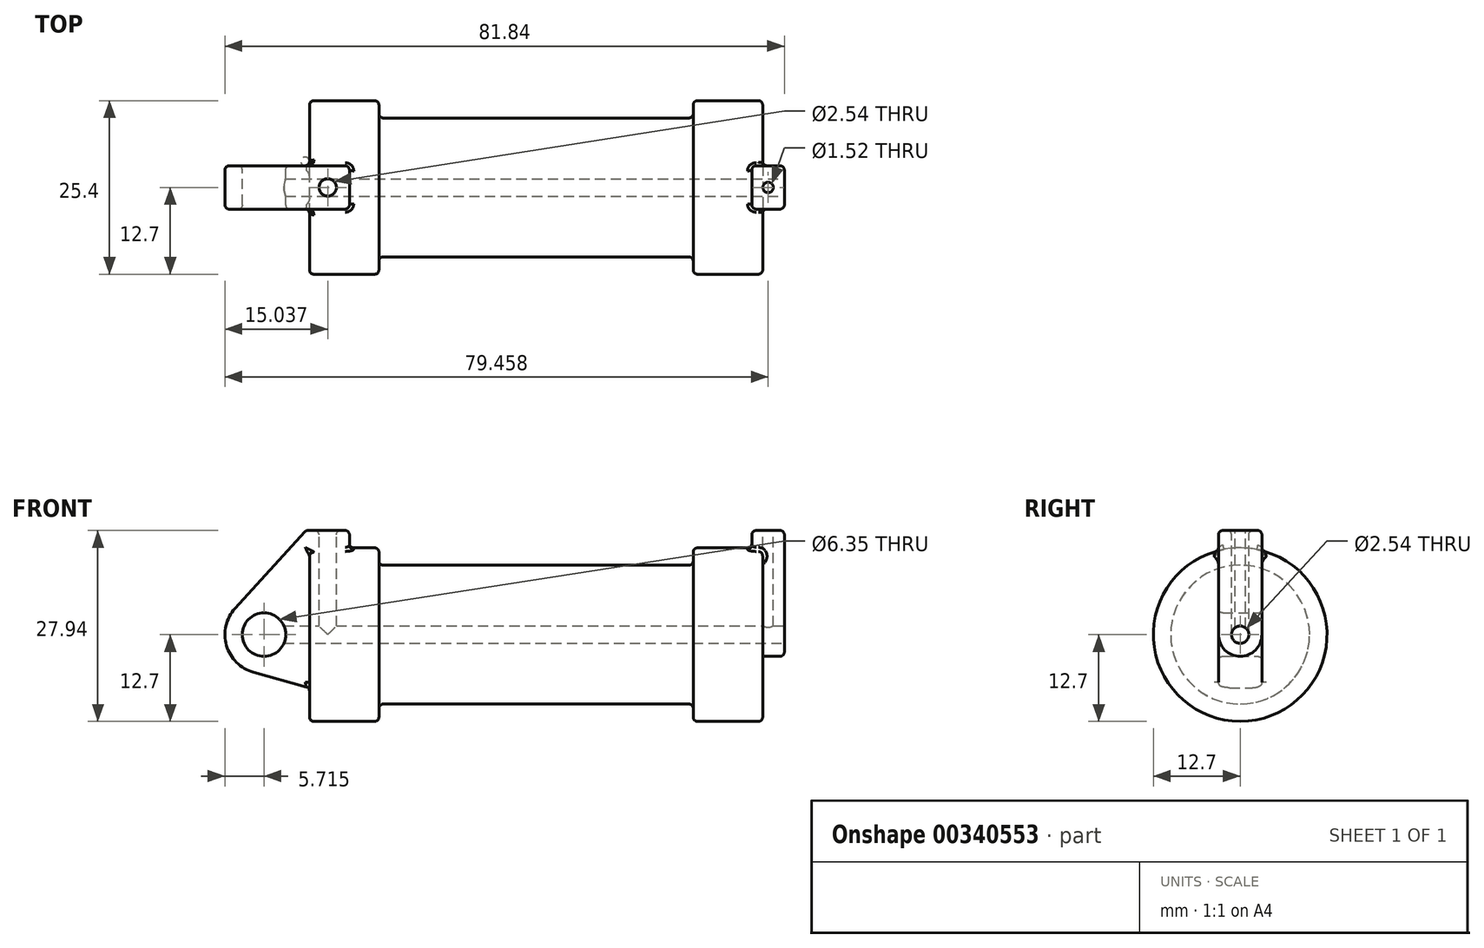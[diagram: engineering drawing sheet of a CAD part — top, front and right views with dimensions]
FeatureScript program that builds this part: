
annotation { "Feature Type Name" : "Feature", "Feature Type Description" : "" }
export const myFeature = defineFeature(function(context is Context, id is Id, definition is map)
    precondition{}
    {
        {
            var Q0;
            Q0=qCreatedBy(makeId("Front.planeOp"),FACE);
            var sketch = newSketch(context, id + "F0", { "sketchPlane" : qUnion([Q0])});
            skLineSegment(sketch, "E0", {"start": v(0, 0) * mm, "end": v(0, 12.7) * mm});
            skLineSegment(sketch, "E1", {"start": v(0, 12.7) * mm, "end": v(10.16, 12.7) * mm});
            skLineSegment(sketch, "E2", {"start": v(10.16, 12.7) * mm, "end": v(10.16, 10.16) * mm});
            skLineSegment(sketch, "E3", {"start": v(10.16, 10.16) * mm, "end": v(56.13, 10.16) * mm});
            skLineSegment(sketch, "E4", {"start": v(56.13, 10.16) * mm, "end": v(56.13, 12.7) * mm});
            skLineSegment(sketch, "E5", {"start": v(56.13, 12.7) * mm, "end": v(66.3, 12.7) * mm});
            skLineSegment(sketch, "E6", {"start": v(66.3, 12.7) * mm, "end": v(66.3, 0) * mm});
            skLineSegment(sketch, "E7", {"start": v(66.3, 0) * mm, "end": v(0, 0) * mm});
            skLineSegment(sketch, "E8", {"start": v(5.84, 15.24) * mm, "end": v(-0.5, 15.24) * mm});
            skLineSegment(sketch, "E9", {"start": v(-0.5, 15.24) * mm, "end": v(-10.88, 3.85) * mm});
            skLineSegment(sketch, "E10", {"start": v(0, 0) * mm, "end": v(-6.65, 0) * mm});
            skCircle(sketch, "E11", {"center": v(-6.65, 0) * mm, "radius": 5.72 * mm});
            skCircle(sketch, "E12", {"center": v(-6.65, 0) * mm, "radius": 3.18 * mm});
            skLineSegment(sketch, "E13", {"start": v(5.84, 15.24) * mm, "end": v(5.84, -9.4) * mm});
            skLineSegment(sketch, "E14", {"start": v(5.84, -9.4) * mm, "end": v(-8.18, -5.5) * mm});
            skSolve(sketch);
        }
        {
            var Q0;
            {var subQ0=sQuery(id+"F0.wireOp",EDGE,"E2");Q0=makeQuery(id+"F0.imprint","IMPRINT",FACE,{"disambiguationData":[TD([[makeQuery(id+"F0.imprint","IMPRINT",EDGE,{"derivedFrom":subQ0}),-1.0]])]});}
            var Q1;
            {var subQ0=sQuery(id+"F0.wireOp",EDGE,"E0");Q1=makeQuery(id+"F0.imprint","IMPRINT",FACE,{"disambiguationData":[TD([[makeQuery(id+"F0.imprint","IMPRINT",EDGE,{"derivedFrom":subQ0}),-1.0]])]});}
            var Q2;
            Q2=sQuery(id+"F0.wireOp",EDGE,"E7");
            revolve(context, id + "F1", {"entities" : qUnion([Q0, Q1]), "axis" : qUnion([Q2]), "revolveType" : RevolveType.FULL});
        }
        {
            var Q0;
            {var subQ0=sQuery(id+"F0.wireOp",EDGE,"E14");Q0=makeQuery(id+"F0.imprint","IMPRINT",FACE,{"disambiguationData":[TD([[makeQuery(id+"F0.imprint","IMPRINT",EDGE,{"derivedFrom":subQ0}),-1.0]])]});}
            var Q1;
            {var subQ0=sQuery(id+"F0.wireOp",EDGE,"E0");Q1=makeQuery(id+"F0.imprint","IMPRINT",FACE,{"disambiguationData":[TD([[makeQuery(id+"F0.imprint","IMPRINT",EDGE,{"derivedFrom":subQ0}),-1.0]])]});}
            var Q2;
            {var subQ1=sQuery(id+"F0.wireOp",EDGE,"E0");Q2=makeQuery(id+"F0.imprint","IMPRINT",FACE,{"disambiguationData":[TD([[makeQuery(id+"F0.imprint","IMPRINT",EDGE,{"derivedFrom":subQ1}),1.0]])]});}
            var Q3;
            {var subQ5=sQuery(id+"F0.wireOp",EDGE,"E12");Q3=makeQuery(id+"F0.imprint","IMPRINT",FACE,{"disambiguationData":[TD([[makeQuery(id+"F0.imprint","IMPRINT",EDGE,{"derivedFrom":subQ5}),-1.0]])]});}
            extrude(context, id + "F2", {"entities" : qUnion([Q0, Q1, Q2, Q3]), "operationType" : NewBodyOperationType.ADD, "endBound" : BoundingType.SYMMETRIC, "depth" : 6.35 * mm});
        }
        {
            var Q0;
            Q0=makeQuery(id+"F1.opRevolve","SWEPT_FACE",FACE,{"disambiguationData":[OSD([sQuery(id+"F0.wireOp",EDGE,"E6")])]});
            var sketch = newSketch(context, id + "F3", { "sketchPlane" : qUnion([Q0])});
            skArc(sketch, "E15", {"start": v(-3.18, 0) * mm, "mid": v(0, -3.18) * mm, "end": v(3.18, 0) * mm});
            skLineSegment(sketch, "E16.0", {"start": v(3.18, 15.24) * mm, "end": v(3.18, 0) * mm});
            skLineSegment(sketch, "E17.0", {"start": v(-3.18, 15.24) * mm, "end": v(3.17, 15.24) * mm});
            skLineSegment(sketch, "E18.0", {"start": v(-3.18, 15.24) * mm, "end": v(-3.18, 0) * mm});
            skPoint(sketch, "E19.orphan", {"position": v(-3.18, 12.3) * mm});
            skPoint(sketch, "E20.orphan", {"position": v(3.18, 12.3) * mm});
            skSolve(sketch);
        }
        {
            var Q0;
            {var subQ0=sQuery(id+"F3.wireOp",EDGE,"E15");Q0=makeQuery(id+"F3.imprint","IMPRINT",FACE,{"disambiguationData":[TD([[makeQuery(id+"F3.imprint","IMPRINT",EDGE,{"derivedFrom":subQ0}),1.0]])]});}
            var Q1;
            {var subQ0=sQuery(id+"F3.wireOp",EDGE,"E17.0");Q1=makeQuery(id+"F3.imprint","IMPRINT",FACE,{"disambiguationData":[TD([[makeQuery(id+"F3.imprint","IMPRINT",EDGE,{"derivedFrom":subQ0}),-1.0]])]});}
            extrude(context, id + "F4", {"entities" : qUnion([Q0, Q1]), "operationType" : NewBodyOperationType.ADD, "depth" : 3.17 * mm});
        }
        {
            var Q0;
            Q0=makeQuery(id+"F4.opExtrude","CAP_FACE",FACE,{"disambiguationData":[OSD([sQuery(id+"F3.wireOp",EDGE,"E15"),sQuery(id+"F3.wireOp",EDGE,"E16.0"),sQuery(id+"F3.wireOp",EDGE,"E17.0"),sQuery(id+"F3.wireOp",EDGE,"E18.0")])],"isStart":true});
            extrude(context, id + "F5", {"entities" : qUnion([Q0]), "operationType" : NewBodyOperationType.ADD, "depth" : 1.59 * mm});
        }
        {
            var Q0;
            Q0=makeQuery(id+"F2.opExtrude","SWEPT_FACE",FACE,{"disambiguationData":[OSD([sQuery(id+"F0.wireOp",EDGE,"E8")])]});
            var sketch = newSketch(context, id + "F6", { "sketchPlane" : qUnion([Q0])});
            skCircle(sketch, "E21", {"center": v(2.67, 0) * mm, "radius": 1.27 * mm});
            skPoint(sketch, "E21.centerSnap0", {"position": v(5.84, 0) * mm});
            skPoint(sketch, "E21.centerSnap1", {"position": v(2.67, 3.18) * mm});
            skSolve(sketch);
        }
        {
            var Q0;
            Q0=makeQuery(id+"F6.imprint","IMPRINT",FACE,{"disambiguationData":[TD([[makeQuery(id+"F6.imprint","IMPRINT",EDGE,{"derivedFrom":sQuery(id+"F6.wireOp",EDGE,"E21")}),1.0]])]});
            extrude(context, id + "F7", {"entities" : qUnion([Q0]), "operationType" : NewBodyOperationType.REMOVE, "oppositeDirection" : true, "depth" : 15.24 * mm});
        }
        {
            var Q0;
            {var subQ0=sQuery(id+"F3.wireOp",EDGE,"E17.0");Q0=makeQuery(id+"F5.boolean.opBoolean","MERGE",FACE,{"derivedFrom":[makeQuery(id+"F4.opExtrude","SWEPT_FACE",FACE,{"disambiguationData":[OSD([subQ0])]}),makeQuery(id+"F5.opExtrude","SWEPT_FACE",FACE,{"disambiguationData":[OSD([subQ0])]})]});}
            var sketch = newSketch(context, id + "F8", { "sketchPlane" : qUnion([Q0])});
            skCircle(sketch, "E22", {"center": v(67.09, 0) * mm, "radius": 0.76 * mm});
            skPoint(sketch, "E22.centerSnap0", {"position": v(69.47, 0) * mm});
            skPoint(sketch, "E22.centerSnap1", {"position": v(67.09, 3.18) * mm});
            skSolve(sketch);
        }
        {
            var Q0;
            Q0=makeQuery(id+"F8.imprint","IMPRINT",FACE,{"disambiguationData":[TD([[makeQuery(id+"F8.imprint","IMPRINT",EDGE,{"derivedFrom":sQuery(id+"F8.wireOp",EDGE,"E22")}),1.0]])]});
            extrude(context, id + "F9", {"entities" : qUnion([Q0]), "operationType" : NewBodyOperationType.REMOVE, "oppositeDirection" : true, "depth" : 15.06 * mm});
        }
        {
            var Q0;
            Q0=makeQuery(id+"F4.opExtrude","CAP_FACE",FACE,{"disambiguationData":[OSD([sQuery(id+"F3.wireOp",EDGE,"E15"),sQuery(id+"F3.wireOp",EDGE,"E16.0"),sQuery(id+"F3.wireOp",EDGE,"E17.0"),sQuery(id+"F3.wireOp",EDGE,"E18.0")])],"isStart":false});
            var sketch = newSketch(context, id + "F10", { "sketchPlane" : qUnion([Q0])});
            skCircle(sketch, "E23", {"center": v(0, 0) * mm, "radius": 1.27 * mm});
            skSolve(sketch);
        }
        {
            var Q0;
            Q0=makeQuery(id+"F10.imprint","IMPRINT",FACE,{"disambiguationData":[TD([[makeQuery(id+"F10.imprint","IMPRINT",EDGE,{"derivedFrom":sQuery(id+"F10.wireOp",EDGE,"E23")}),1.0]])]});
            extrude(context, id + "F11", {"entities" : qUnion([Q0]), "operationType" : NewBodyOperationType.REMOVE, "oppositeDirection" : true, "depth" : 76.2 * mm});
        }
        {
            var Q0;
            {var subQ0=sQuery(id+"F3.wireOp",EDGE,"E16.0");Q0=makeQuery(id+"F4.boolean.opBoolean","SPLIT",EDGE,{"disambiguationData":[topologyDisambiguationEdgeConnected([makeQuery(id+"F1.opRevolve","SWEPT_FACE",FACE,{"disambiguationData":[OSD([sQuery(id+"F0.wireOp",EDGE,"E6")])]})])],"derivedFrom":makeQuery(id+"F4.opExtrude","CAP_EDGE",EDGE,{"disambiguationData":[OSD([subQ0])],"isStart":true})});}
            var Q1;
            Q1=makeQuery(id+"F4.opExtrude","CAP_EDGE",EDGE,{"disambiguationData":[OSD([sQuery(id+"F3.wireOp",EDGE,"E16.0")])],"isStart":false});
            var Q2;
            {var subQ0=sQuery(id+"F3.wireOp",EDGE,"E17.0");var subQ1=sQuery(id+"F3.wireOp",EDGE,"E16.0");Q2=makeQuery(id+"F5.boolean.opBoolean","MERGE",EDGE,{"derivedFrom":[makeQuery(id+"F4.opExtrude","SWEPT_EDGE",EDGE,{"disambiguationData":[OSD([subQ1,subQ0])]}),makeQuery(id+"F5.opExtrude","SWEPT_EDGE",EDGE,{"disambiguationData":[OSD([subQ1,subQ0])]})]});}
            var Q3;
            Q3=makeQuery(id+"F5.opExtrude","CAP_EDGE",EDGE,{"disambiguationData":[OSD([sQuery(id+"F3.wireOp",EDGE,"E16.0")])],"isStart":false});
            var Q4;
            {var subQ0=sQuery(id+"F3.wireOp",EDGE,"E16.0");var subQ1=sQuery(id+"F3.wireOp",EDGE,"E18.0");var subQ2=sQuery(id+"F3.wireOp",EDGE,"E17.0");var subQ3=sQuery(id+"F3.wireOp",EDGE,"E15");var subQ4=sQuery(id+"F0.wireOp",EDGE,"E6");var subQ5=sQuery(id+"F0.wireOp",EDGE,"E5");Q4=makeQuery(id+"F5.opExtrude","SWEPT_EDGE",EDGE,{"disambiguationData":[OSD([subQ5,subQ4,subQ3,subQ0,subQ2,subQ1]),TDD([makeQuery(id+"F4.boolean.opBoolean","TWEAK_VERTEX",VERTEX,{"derivedFrom":[makeQuery(id+"F1.opRevolve","SWEPT_FACE",FACE,{"disambiguationData":[OSD([subQ5])]}),makeQuery(id+"F1.opRevolve","SWEPT_FACE",FACE,{"disambiguationData":[OSD([subQ4])]}),makeQuery(id+"F4.opExtrude","CAP_FACE",FACE,{"disambiguationData":[OSD([subQ3,subQ0,subQ2,subQ1])],"isStart":true}),makeQuery(id+"F4.opExtrude","SWEPT_FACE",FACE,{"disambiguationData":[OSD([subQ0])]})]})])]});}
            var Q5;
            Q5=makeQuery(id+"F4.opExtrude","CAP_EDGE",EDGE,{"disambiguationData":[OSD([sQuery(id+"F3.wireOp",EDGE,"E17.0")])],"isStart":false});
            var Q6;
            {var subQ0=sQuery(id+"F3.wireOp",EDGE,"E18.0");var subQ1=sQuery(id+"F3.wireOp",EDGE,"E17.0");Q6=makeQuery(id+"F5.boolean.opBoolean","MERGE",EDGE,{"derivedFrom":[makeQuery(id+"F4.opExtrude","SWEPT_EDGE",EDGE,{"disambiguationData":[OSD([subQ1,subQ0])]}),makeQuery(id+"F5.opExtrude","SWEPT_EDGE",EDGE,{"disambiguationData":[OSD([subQ1,subQ0])]})]});}
            var Q7;
            Q7=makeQuery(id+"F5.opExtrude","CAP_EDGE",EDGE,{"disambiguationData":[OSD([sQuery(id+"F3.wireOp",EDGE,"E18.0")])],"isStart":false});
            var Q8;
            {var subQ0=sQuery(id+"F3.wireOp",EDGE,"E18.0");var subQ1=sQuery(id+"F3.wireOp",EDGE,"E17.0");var subQ2=sQuery(id+"F3.wireOp",EDGE,"E16.0");var subQ3=sQuery(id+"F3.wireOp",EDGE,"E15");var subQ4=sQuery(id+"F0.wireOp",EDGE,"E6");var subQ5=sQuery(id+"F0.wireOp",EDGE,"E5");Q8=makeQuery(id+"F5.opExtrude","SWEPT_EDGE",EDGE,{"disambiguationData":[OSD([subQ5,subQ4,subQ3,subQ2,subQ1,subQ0]),TDD([makeQuery(id+"F4.boolean.opBoolean","TWEAK_VERTEX",VERTEX,{"derivedFrom":[makeQuery(id+"F1.opRevolve","SWEPT_FACE",FACE,{"disambiguationData":[OSD([subQ5])]}),makeQuery(id+"F1.opRevolve","SWEPT_FACE",FACE,{"disambiguationData":[OSD([subQ4])]}),makeQuery(id+"F4.opExtrude","CAP_FACE",FACE,{"disambiguationData":[OSD([subQ3,subQ2,subQ1,subQ0])],"isStart":true}),makeQuery(id+"F4.opExtrude","SWEPT_FACE",FACE,{"disambiguationData":[OSD([subQ0])]})]})])]});}
            var Q9;
            Q9=makeQuery(id+"F5.opExtrude","CAP_EDGE",EDGE,{"disambiguationData":[OSD([sQuery(id+"F3.wireOp",EDGE,"E17.0")])],"isStart":false});
            var Q10;
            Q10=makeQuery(id+"F4.opExtrude","CAP_EDGE",EDGE,{"disambiguationData":[OSD([sQuery(id+"F3.wireOp",EDGE,"E15")])],"isStart":false});
            var Q11;
            Q11=makeQuery(id+"F4.opExtrude","CAP_EDGE",EDGE,{"disambiguationData":[OSD([sQuery(id+"F3.wireOp",EDGE,"E15")])],"isStart":true});
            var Q12;
            {var subQ0=sQuery(id+"F3.wireOp",EDGE,"E18.0");Q12=makeQuery(id+"F4.boolean.opBoolean","SPLIT",EDGE,{"disambiguationData":[topologyDisambiguationEdgeConnected([makeQuery(id+"F1.opRevolve","SWEPT_FACE",FACE,{"disambiguationData":[OSD([sQuery(id+"F0.wireOp",EDGE,"E6")])]})])],"derivedFrom":makeQuery(id+"F4.opExtrude","CAP_EDGE",EDGE,{"disambiguationData":[OSD([subQ0])],"isStart":true})});}
            var Q13;
            Q13=makeQuery(id+"F4.opExtrude","CAP_EDGE",EDGE,{"disambiguationData":[OSD([sQuery(id+"F3.wireOp",EDGE,"E18.0")])],"isStart":false});
            fillet(context, id + "F12", {"entities" : qUnion([Q0, Q1, Q2, Q3, Q4, Q5, Q6, Q7, Q8, Q9, Q10, Q11, Q12, Q13]), "radius" : 0.64 * mm, "tangentPropagation" : true, "allowEdgeOverflow" : false});
        }
        {
            var Q0;
            Q0=makeQuery(id+"F2.opExtrude","CAP_FACE",FACE,{"disambiguationData":[OSD([sQuery(id+"F0.wireOp",EDGE,"E8"),sQuery(id+"F0.wireOp",EDGE,"E9"),sQuery(id+"F0.wireOp",EDGE,"E11"),sQuery(id+"F0.wireOp",EDGE,"E12"),sQuery(id+"F0.wireOp",EDGE,"E13"),sQuery(id+"F0.wireOp",EDGE,"E14")])],"isStart":false});
            var Q1;
            Q1=makeQuery(id+"F2.opExtrude","SWEPT_FACE",FACE,{"disambiguationData":[OSD([sQuery(id+"F0.wireOp",EDGE,"E9")])]});
            var Q2;
            Q2=makeQuery(id+"F2.opExtrude","SWEPT_FACE",FACE,{"disambiguationData":[OSD([sQuery(id+"F0.wireOp",EDGE,"E11")])]});
            var Q3;
            Q3=makeQuery(id+"F2.opExtrude","SWEPT_FACE",FACE,{"disambiguationData":[OSD([sQuery(id+"F0.wireOp",EDGE,"E8")])]});
            var Q4;
            Q4=makeQuery(id+"F2.opExtrude","CAP_FACE",FACE,{"disambiguationData":[OSD([sQuery(id+"F0.wireOp",EDGE,"E8"),sQuery(id+"F0.wireOp",EDGE,"E9"),sQuery(id+"F0.wireOp",EDGE,"E11"),sQuery(id+"F0.wireOp",EDGE,"E12"),sQuery(id+"F0.wireOp",EDGE,"E13"),sQuery(id+"F0.wireOp",EDGE,"E14")])],"isStart":true});
            fillet(context, id + "F13", {"entities" : qUnion([Q0, Q1, Q2, Q3, Q4]), "radius" : 0.64 * mm, "tangentPropagation" : true, "allowEdgeOverflow" : false});
        }
        {
            var Q0;
            Q0=makeQuery(id+"F1.opRevolve","SWEPT_FACE",FACE,{"disambiguationData":[OSD([sQuery(id+"F0.wireOp",EDGE,"E3")])]});
            var Q1;
            Q1=makeQuery(id+"F1.opRevolve","SWEPT_FACE",FACE,{"disambiguationData":[OSD([sQuery(id+"F0.wireOp",EDGE,"E5")])]});
            var Q2;
            Q2=makeQuery(id+"F1.opRevolve","SWEPT_FACE",FACE,{"disambiguationData":[OSD([sQuery(id+"F0.wireOp",EDGE,"E1")])]});
            fillet(context, id + "F14", {"entities" : qUnion([Q0, Q1, Q2]), "radius" : 0.64 * mm, "tangentPropagation" : true, "allowEdgeOverflow" : false});
        }
    });
